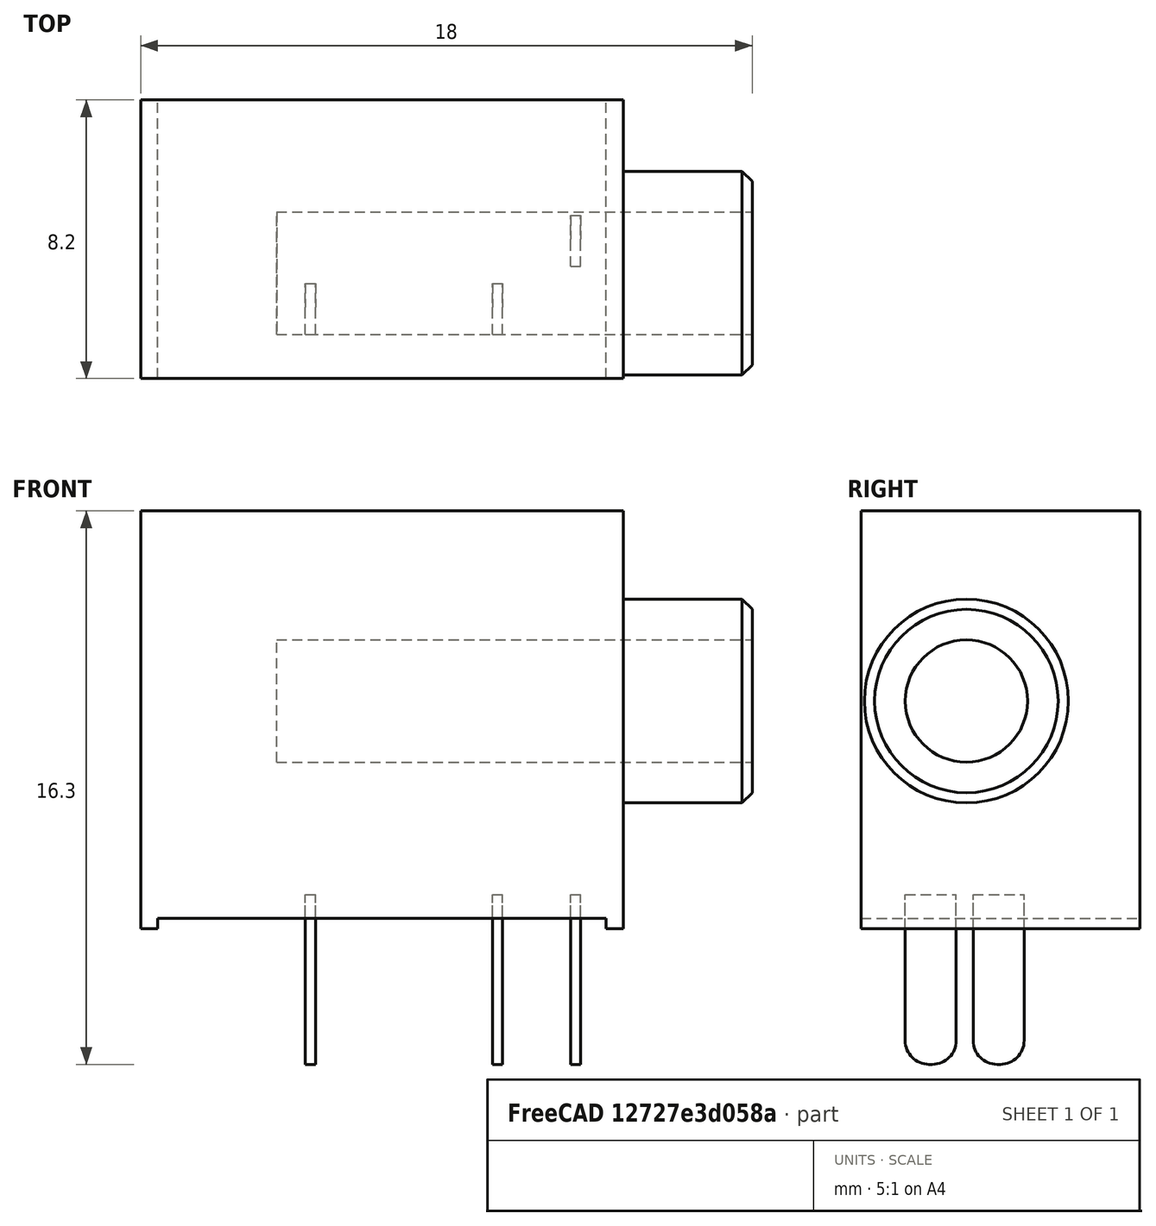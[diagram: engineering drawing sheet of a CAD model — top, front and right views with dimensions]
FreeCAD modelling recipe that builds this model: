
FCSTD DOCUMENT  (FreeCAD 0.16R6706 (Git))
Label: jack-3.5mm-st-215n-04
License: All rights reserved
LicenseURL: http://en.wikipedia.org/wiki/All_rights_reserved
objects: Part::Box×3, Part::Fillet×3, Part::Cylinder×2, Part::MultiFuse×2, Part::Cut×1, Part::Chamfer×1
note: 12 computed .brp shape members not serialized (recipe doc carries the construction recipe); baked Part::Feature solids carry a one-line shape summary decoded from their .brp

FEATURE [Part::Box] Box  label="Cube"
  Height = 12.3
  Length = 14.2
  Width = 8.2
FEATURE [Part::Cylinder] Cylinder
  Angle = 360
  Height = 4
  Placement = pos=(14,3.1,6.7) rot=(0,1,0;1.5708rad)
  Radius = 3
FEATURE [Part::Box] Box001  label="Cube-"
  Height = 12.3
  Length = 13.2
  Placement = pos=(0.5,0,-12) rot=(0,0,1;0rad)
  Width = 8.2
FEATURE [Part::Cylinder] Cylinder001  label="Cylinder-"
  Angle = 360
  Height = 14
  Placement = pos=(4,3.1,6.7) rot=(0,1,0;1.5708rad)
  Radius = 1.8
FEATURE [Part::MultiFuse] Fusion  label="Fusion-"
  Shapes = -> [Cylinder001,Box001]
FEATURE [Part::MultiFuse] Fusion001  label="Fusion+"
  Shapes = -> [Box,Cylinder]
FEATURE [Part::Cut] Cut
  Base = -> Fusion001
  Tool = -> Fusion
FEATURE [Part::Box] Box002  label="Cube001"
  Height = 5
  Length = 0.3
  Placement = pos=(12.65,3.3,-4) rot=(0,0,1;0rad)
  Width = 1.5
FEATURE [Part::Fillet] Fillet  label="Terminal1"
  Base = -> Box002
  Edges = 2 edges r=0.7: [Edge9,Edge11]
FEATURE [Part::Fillet] Fillet001  label="Terminal2"
  Base = -> Box002
  Edges = 2 edges r=0.7: [Edge9,Edge11]
  Placement = pos=(-2.3,-2,0) rot=(0,0,1;0rad)
FEATURE [Part::Fillet] Fillet002  label="Terminal3"
  Base = -> Box002
  Edges = 2 edges r=0.7: [Edge9,Edge11]
  Placement = pos=(-7.8,-2,0) rot=(0,0,1;0rad)
FEATURE [Part::Chamfer] Chamfer
  Base = -> Cut
  Edges = 1 edges r=0.3: [Edge27]
